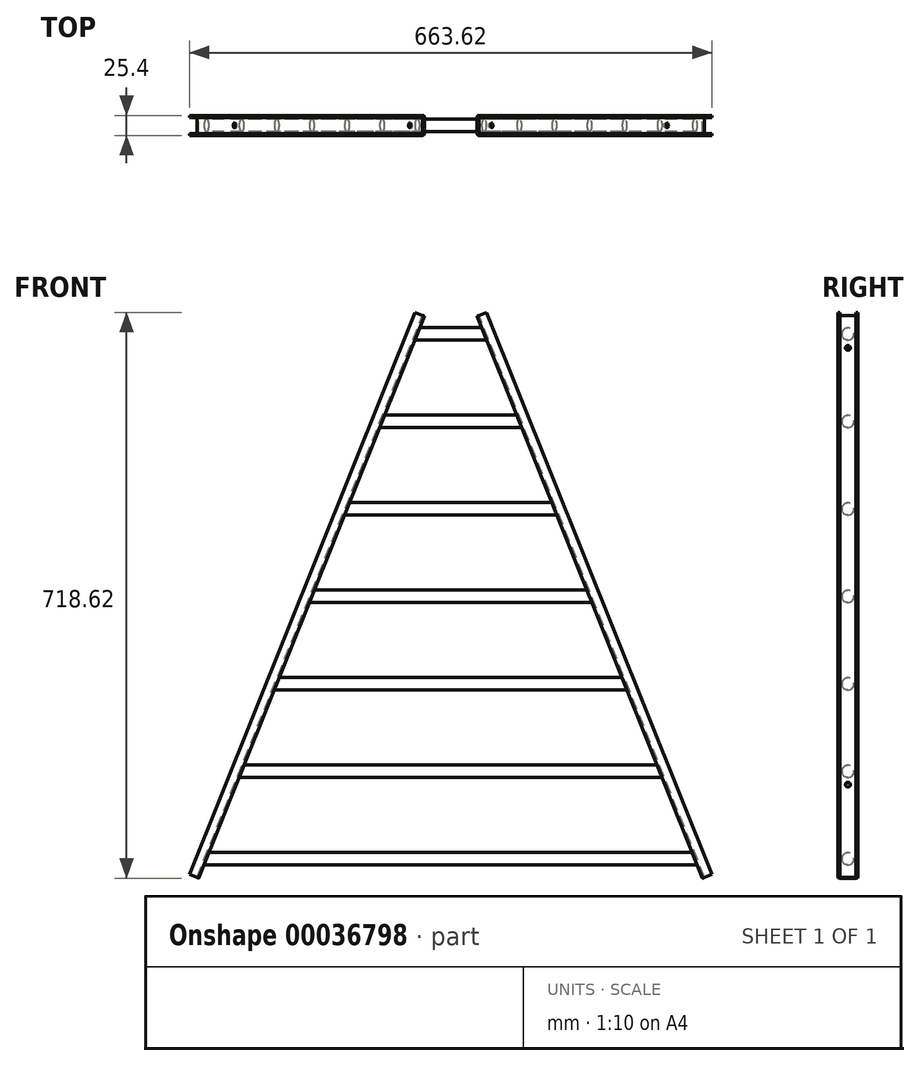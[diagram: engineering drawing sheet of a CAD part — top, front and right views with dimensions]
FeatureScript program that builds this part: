
annotation { "Feature Type Name" : "Feature", "Feature Type Description" : "" }
export const myFeature = defineFeature(function(context is Context, id is Id, definition is map)
    precondition{}
    {
        {
            var Q0;
            Q0=qCreatedBy(makeId("Front.planeOp"),FACE);
            var sketch = newSketch(context, id + "F0", { "sketchPlane" : qUnion([Q0])});
            skLineSegment(sketch, "E0", {"start": v(-3.7, 0) * mm, "end": v(0, 0) * mm});
            skLineSegment(sketch, "E1", {"start": v(0, 0) * mm, "end": v(3.7, 0) * mm});
            skLineSegment(sketch, "E2", {"start": v(-3.7, 0) * mm, "end": v(-454.08, -1121.57) * mm});
            skLineSegment(sketch, "E3", {"start": v(3.7, 0) * mm, "end": v(454.08, -1121.57) * mm});
            skLineSegment(sketch, "E4", {"start": v(-454.08, -1121.57) * mm, "end": v(0, -1121.57) * mm});
            skLineSegment(sketch, "E5", {"start": v(0, -1121.57) * mm, "end": v(454.08, -1121.57) * mm});
            skPoint(sketch, "E6.orphan", {"position": v(-648.72, -738.24) * mm});
            skLineSegment(sketch, "E7", {"start": v(-661.17, -873.2) * mm, "end": v(940.26, -873.2) * mm});
            skLineSegment(sketch, "E8.0.1.0", {"start": v(-661.17, -770.01) * mm, "end": v(940.26, -770.01) * mm});
            skLineSegment(sketch, "E8.1.0.0", {"start": v(-610.38, -873.2) * mm, "end": v(991.05, -873.2) * mm});
            skLineSegment(sketch, "E8.1.1.0", {"start": v(-610.38, -770.01) * mm, "end": v(991.05, -770.01) * mm});
            skLineSegment(sketch, "E8.direction1", {"start": v(-661.17, -873.2) * mm, "end": v(-610.38, -873.2) * mm, "construction": true});
            skLineSegment(sketch, "E8.direction2", {"start": v(-661.17, -873.2) * mm, "end": v(-661.17, -770.01) * mm, "construction": true});
            skLineSegment(sketch, "E9.0.1.0", {"start": v(-610.38, -658.89) * mm, "end": v(991.05, -658.89) * mm});
            skLineSegment(sketch, "E9.0.2.0", {"start": v(-610.38, -547.76) * mm, "end": v(991.05, -547.76) * mm});
            skLineSegment(sketch, "E9.0.3.0", {"start": v(-610.38, -436.64) * mm, "end": v(991.05, -436.64) * mm});
            skLineSegment(sketch, "E9.0.4.0", {"start": v(-610.38, -325.51) * mm, "end": v(991.05, -325.51) * mm});
            skLineSegment(sketch, "E9.0.5.0", {"start": v(-610.38, -214.39) * mm, "end": v(991.05, -214.39) * mm});
            skLineSegment(sketch, "E9.0.6.0", {"start": v(-610.38, -103.26) * mm, "end": v(991.05, -103.26) * mm});
            skLineSegment(sketch, "E9.1.0.0", {"start": v(-584.98, -770.01) * mm, "end": v(1016.45, -770.01) * mm});
            skLineSegment(sketch, "E9.1.1.0", {"start": v(-584.98, -658.89) * mm, "end": v(1016.45, -658.89) * mm});
            skLineSegment(sketch, "E9.1.2.0", {"start": v(-584.98, -547.76) * mm, "end": v(1016.45, -547.76) * mm});
            skLineSegment(sketch, "E9.1.3.0", {"start": v(-584.98, -436.64) * mm, "end": v(1016.45, -436.64) * mm});
            skLineSegment(sketch, "E9.1.4.0", {"start": v(-584.98, -325.51) * mm, "end": v(1016.45, -325.51) * mm});
            skLineSegment(sketch, "E9.1.5.0", {"start": v(-584.98, -214.39) * mm, "end": v(1016.45, -214.39) * mm});
            skLineSegment(sketch, "E9.1.6.0", {"start": v(-584.98, -103.26) * mm, "end": v(1016.45, -103.26) * mm});
            skLineSegment(sketch, "E9.2.0.0", {"start": v(-559.58, -770.01) * mm, "end": v(1041.85, -770.01) * mm});
            skLineSegment(sketch, "E9.2.1.0", {"start": v(-559.58, -658.89) * mm, "end": v(1041.85, -658.89) * mm});
            skLineSegment(sketch, "E9.2.2.0", {"start": v(-559.58, -547.76) * mm, "end": v(1041.85, -547.76) * mm});
            skLineSegment(sketch, "E9.2.3.0", {"start": v(-559.58, -436.64) * mm, "end": v(1041.85, -436.64) * mm});
            skLineSegment(sketch, "E9.2.4.0", {"start": v(-559.58, -325.51) * mm, "end": v(1041.85, -325.51) * mm});
            skLineSegment(sketch, "E9.2.5.0", {"start": v(-559.58, -214.39) * mm, "end": v(1041.85, -214.39) * mm});
            skLineSegment(sketch, "E9.2.6.0", {"start": v(-559.58, -103.26) * mm, "end": v(1041.85, -103.26) * mm});
            skLineSegment(sketch, "E9.direction1", {"start": v(-610.38, -770.01) * mm, "end": v(-584.98, -770.01) * mm, "construction": true});
            skLineSegment(sketch, "E9.direction2", {"start": v(-610.38, -770.01) * mm, "end": v(-610.38, -658.89) * mm, "construction": true});
            skPoint(sketch, "E10", {"position": v(354.35, -873.2) * mm});
            skPoint(sketch, "E11", {"position": v(45.17, -103.26) * mm});
            skPoint(sketch, "E12", {"position": v(312.91, -770.01) * mm});
            skSolve(sketch);
        }
        {
            var Q0;
            Q0=sQuery(id+"F0.wireOp",VERTEX,"E12");
            var Q1;
            Q1=sQuery(id+"F0.wireOp",EDGE,"E3");
            cPlane(context, id + "F1", {"entities" : qUnion([Q0, Q1]), "cplaneType" : CPlaneType.LINE_POINT, "offset" : 152.4 * mm, "width" : 152.4 * mm, "height" : 152.4 * mm});
        }
        {
            var Q0;
            Q0=qCreatedBy(id+"F1.planeOp",FACE);
            var sketch = newSketch(context, id + "F2", { "sketchPlane" : qUnion([Q0])});
            skPoint(sketch, "E13.0", {"position": v(3.44, 0) * mm});
            skLineSegment(sketch, "E14", {"start": v(3.44, 0) * mm, "end": v(3.44, 10.16) * mm});
            skLineSegment(sketch, "E15", {"start": v(3.44, 10.16) * mm, "end": v(13.6, 10.16) * mm});
            skLineSegment(sketch, "E16", {"start": v(13.6, 10.16) * mm, "end": v(13.6, 12.7) * mm});
            skLineSegment(sketch, "E17", {"start": v(13.6, 12.7) * mm, "end": v(3.44, 12.7) * mm});
            skLineSegment(sketch, "E18", {"start": v(0.9, 10.16) * mm, "end": v(0.9, 0) * mm});
            skPoint(sketch, "E19.visualSharp", {"position": v(0.9, 12.7) * mm});
            skArc(sketch, "E19.filletArc", {"start": v(3.44, 12.7) * mm, "mid": v(1.65, 11.96) * mm, "end": v(0.9, 10.16) * mm});
            skLineSegment(sketch, "E20.MirrorCS", {"start": v(3.44, -10.16) * mm, "end": v(13.6, -10.16) * mm});
            skLineSegment(sketch, "E21.MirrorCS", {"start": v(3.44, 0) * mm, "end": v(3.44, -10.16) * mm});
            skLineSegment(sketch, "E22.MirrorCS", {"start": v(13.6, -10.16) * mm, "end": v(13.6, -12.7) * mm});
            skLineSegment(sketch, "E23.MirrorCS", {"start": v(13.6, -12.7) * mm, "end": v(3.44, -12.7) * mm});
            skArc(sketch, "E24.MirrorCS", {"start": v(3.44, -12.7) * mm, "mid": v(1.65, -11.96) * mm, "end": v(0.9, -10.16) * mm});
            skLineSegment(sketch, "E25.MirrorCS", {"start": v(0.9, -10.16) * mm, "end": v(0.9, 0) * mm});
            skSolve(sketch);
        }
        {
            var Q0;
            Q0 = qSketchRegion(id + "F2", true);
            extrude(context, id + "F3", {"entities" : qUnion([Q0]), "depth" : 25.4 * mm, "hasSecondDirection" : true, "secondDirectionOppositeDirection" : true, "secondDirectionDepth" : 743.9 * mm});
        }
        {
            var Q0;
            Q0=makeQuery(id+"F3.opExtrude","SWEPT_FACE",FACE,{"disambiguationData":[OSD([sQuery(id+"F2.wireOp",EDGE,"E18"),sQuery(id+"F2.wireOp",EDGE,"E25.MirrorCS")])]});
            var sketch = newSketch(context, id + "F4", { "sketchPlane" : qUnion([Q0])});
            skCircle(sketch, "E26", {"center": v(0, -131.72) * mm, "radius": 3.18 * mm});
            skCircle(sketch, "E27", {"center": v(0, -729.56) * mm, "radius": 3.18 * mm});
            skSolve(sketch);
        }
        {
            var Q0;
            Q0 = qSketchRegion(id + "F4", true);
            extrude(context, id + "F5", {"entities" : qUnion([Q0]), "operationType" : NewBodyOperationType.REMOVE, "endBound" : BoundingType.UP_TO_NEXT, "oppositeDirection" : true, "depth" : 25.4 * mm});
        }
        {
            var Q0;
            Q0=makeQuery(id+"F3.opExtrude","SWEPT_BODY",BODY,{"disambiguationData":[OSD([sQuery(id+"F2.wireOp",EDGE,"E14"),sQuery(id+"F2.wireOp",EDGE,"E15"),sQuery(id+"F2.wireOp",EDGE,"E16"),sQuery(id+"F2.wireOp",EDGE,"E17"),sQuery(id+"F2.wireOp",EDGE,"E18"),sQuery(id+"F2.wireOp",EDGE,"E19.filletArc"),sQuery(id+"F2.wireOp",EDGE,"E20.MirrorCS"),sQuery(id+"F2.wireOp",EDGE,"E21.MirrorCS"),sQuery(id+"F2.wireOp",EDGE,"E22.MirrorCS"),sQuery(id+"F2.wireOp",EDGE,"E23.MirrorCS"),sQuery(id+"F2.wireOp",EDGE,"E24.MirrorCS"),sQuery(id+"F2.wireOp",EDGE,"E25.MirrorCS")])]});
            var Q1;
            Q1=qCreatedBy(makeId("Right.planeOp"),FACE);
            mirror(context, id + "F6", {"entities" : qUnion([Q0]), "mirrorPlane" : qUnion([Q1])});
        }
        {
            var Q0;
            Q0=qCreatedBy(makeId("Right.planeOp"),FACE);
            var sketch = newSketch(context, id + "F7", { "sketchPlane" : qUnion([Q0])});
            skPoint(sketch, "E28.0", {"position": v(0, -103.26) * mm});
            skPoint(sketch, "E29.0", {"position": v(0, -214.39) * mm});
            skPoint(sketch, "E30.0", {"position": v(0, -325.51) * mm});
            skPoint(sketch, "E31.0", {"position": v(0, -436.64) * mm});
            skPoint(sketch, "E32.0", {"position": v(0, -547.76) * mm});
            skPoint(sketch, "E33.0", {"position": v(0, -658.89) * mm});
            skPoint(sketch, "E34.0", {"position": v(0, -770.01) * mm});
            skCircle(sketch, "E35", {"center": v(0, -103.26) * mm, "radius": 7.94 * mm});
            skCircle(sketch, "E36", {"center": v(0, -214.39) * mm, "radius": 7.94 * mm});
            skCircle(sketch, "E37", {"center": v(0, -325.51) * mm, "radius": 7.94 * mm});
            skCircle(sketch, "E38", {"center": v(0, -436.64) * mm, "radius": 7.94 * mm});
            skCircle(sketch, "E39", {"center": v(0, -547.76) * mm, "radius": 7.94 * mm});
            skCircle(sketch, "E40", {"center": v(0, -658.89) * mm, "radius": 7.94 * mm});
            skCircle(sketch, "E41", {"center": v(0, -770.01) * mm, "radius": 7.94 * mm});
            skSolve(sketch);
        }
        {
            var Q0;
            Q0 = qSketchRegion(id + "F7", true);
            extrude(context, id + "F8", {"entities" : qUnion([Q0]), "operationType" : NewBodyOperationType.ADD, "endBound" : BoundingType.UP_TO_NEXT, "depth" : 25.4 * mm, "hasSecondDirection" : true, "secondDirectionBound" : SecondDirectionBoundingType.UP_TO_NEXT, "secondDirectionOppositeDirection" : true, "secondDirectionDepth" : 25.4 * mm});
        }
    });
